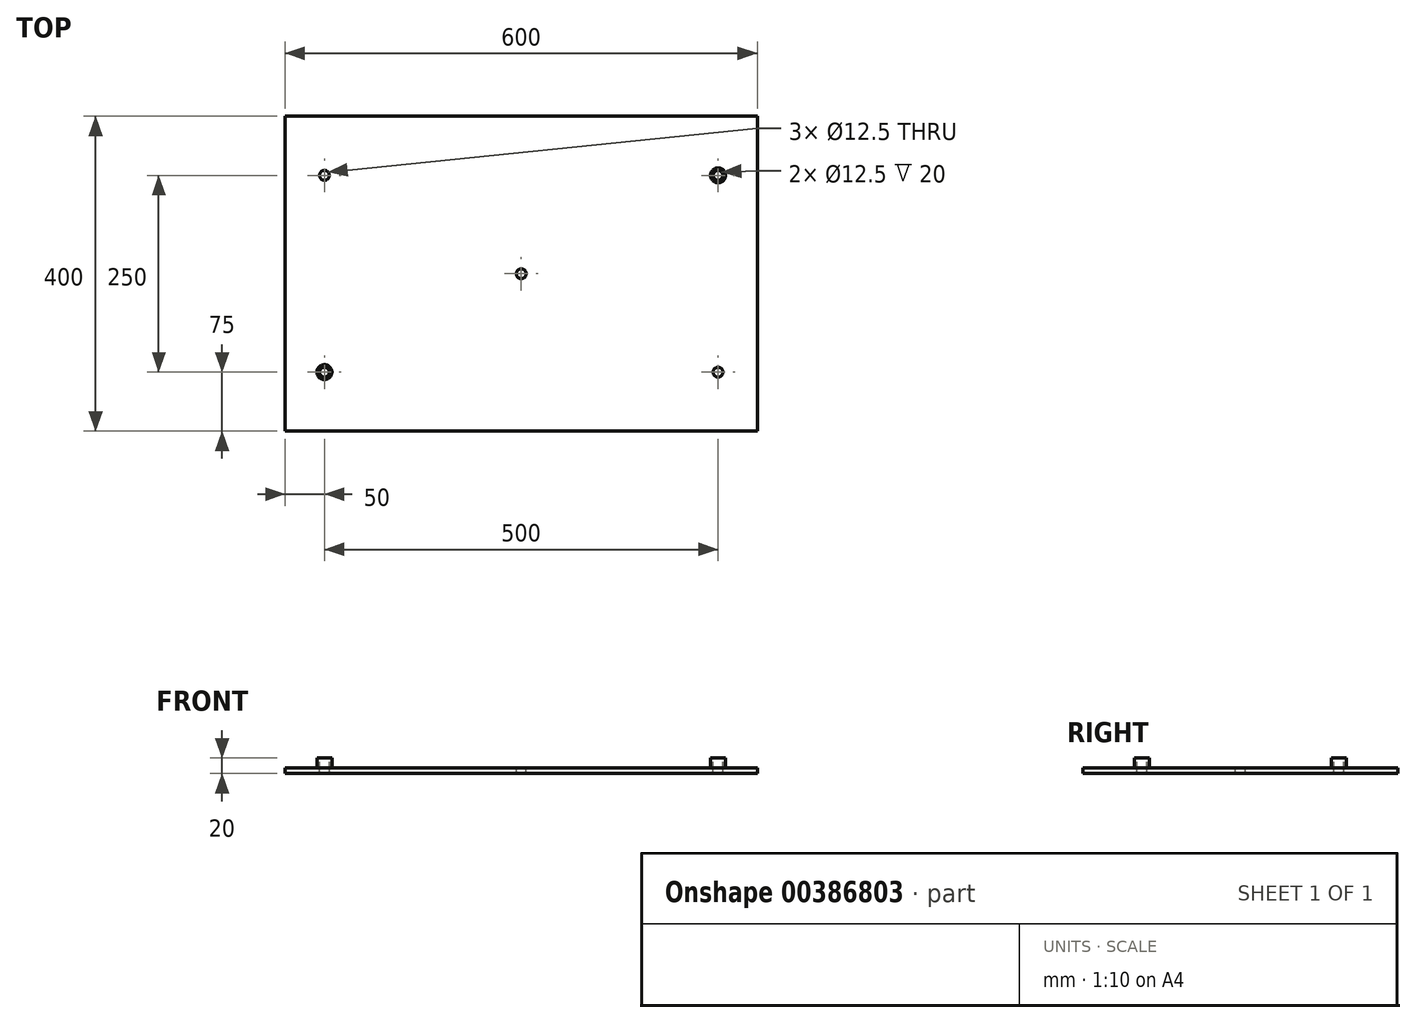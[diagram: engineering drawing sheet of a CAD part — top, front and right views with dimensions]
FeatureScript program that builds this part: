
annotation { "Feature Type Name" : "Feature", "Feature Type Description" : "" }
export const myFeature = defineFeature(function(context is Context, id is Id, definition is map)
    precondition{}
    {
        {
            var Q0;
            Q0=qCreatedBy(makeId("Top.planeOp"),FACE);
            var sketch = newSketch(context, id + "F0", { "sketchPlane" : qUnion([Q0])});
            skLineSegment(sketch, "E0.bottom", {"start": v(300, -200) * mm, "end": v(-300, -200) * mm});
            skLineSegment(sketch, "E0.top", {"start": v(300, 200) * mm, "end": v(-300, 200) * mm});
            skLineSegment(sketch, "E0.left", {"start": v(300, -200) * mm, "end": v(300, 200) * mm});
            skLineSegment(sketch, "E0.right", {"start": v(-300, -200) * mm, "end": v(-300, 200) * mm});
            skPoint(sketch, "E0.middle", {"position": v(0, 0) * mm});
            skSolve(sketch);
        }
        {
            var Q0;
            Q0=makeQuery(id+"F0.imprint","IMPRINT",FACE,{"disambiguationData":[TD([[makeQuery(id+"F0.imprint","IMPRINT",EDGE,{"derivedFrom":sQuery(id+"F0.wireOp",EDGE,"E0.bottom")}),-1.0]])]});
            extrude(context, id + "F1", {"entities" : qUnion([Q0]), "depth" : 20 * mm});
        }
        {
            var Q0;
            Q0=makeQuery(id+"F1.opExtrude","CAP_FACE",FACE,{"disambiguationData":[OSD([sQuery(id+"F0.wireOp",EDGE,"E0.bottom"),sQuery(id+"F0.wireOp",EDGE,"E0.top"),sQuery(id+"F0.wireOp",EDGE,"E0.left"),sQuery(id+"F0.wireOp",EDGE,"E0.right")])],"isStart":false});
            var sketch = newSketch(context, id + "F2", { "sketchPlane" : qUnion([Q0])});
            skCircle(sketch, "E1", {"center": v(-250, 125) * mm, "radius": 6.25 * mm});
            skCircle(sketch, "E2", {"center": v(-250, -125) * mm, "radius": 6.25 * mm});
            skCircle(sketch, "E3", {"center": v(0, 0) * mm, "radius": 6.25 * mm});
            skCircle(sketch, "E4", {"center": v(250, 125) * mm, "radius": 6.25 * mm});
            skCircle(sketch, "E5", {"center": v(250, -125) * mm, "radius": 6.25 * mm});
            skSolve(sketch);
        }
        {
            var Q0;
            Q0=makeQuery(id+"F2.imprint","IMPRINT",FACE,{"disambiguationData":[TD([[makeQuery(id+"F2.imprint","IMPRINT",EDGE,{"derivedFrom":sQuery(id+"F2.wireOp",EDGE,"E1")}),1.0]])]});
            var Q1;
            Q1=makeQuery(id+"F2.imprint","IMPRINT",FACE,{"disambiguationData":[TD([[makeQuery(id+"F2.imprint","IMPRINT",EDGE,{"derivedFrom":sQuery(id+"F2.wireOp",EDGE,"E2")}),1.0]])]});
            var Q2;
            Q2=makeQuery(id+"F2.imprint","IMPRINT",FACE,{"disambiguationData":[TD([[makeQuery(id+"F2.imprint","IMPRINT",EDGE,{"derivedFrom":sQuery(id+"F2.wireOp",EDGE,"E4")}),1.0]])]});
            var Q3;
            Q3=makeQuery(id+"F2.imprint","IMPRINT",FACE,{"disambiguationData":[TD([[makeQuery(id+"F2.imprint","IMPRINT",EDGE,{"derivedFrom":sQuery(id+"F2.wireOp",EDGE,"E5")}),1.0]])]});
            var Q4;
            Q4=makeQuery(id+"F2.imprint","IMPRINT",FACE,{"disambiguationData":[TD([[makeQuery(id+"F2.imprint","IMPRINT",EDGE,{"derivedFrom":sQuery(id+"F2.wireOp",EDGE,"E3")}),1.0]])]});
            extrude(context, id + "F3", {"entities" : qUnion([Q0, Q1, Q2, Q3, Q4]), "operationType" : NewBodyOperationType.REMOVE, "oppositeDirection" : true, "depth" : 25 * mm});
        }
        {
            var Q0;
            Q0=makeQuery(id+"F1.opExtrude","CAP_FACE",FACE,{"disambiguationData":[OSD([sQuery(id+"F0.wireOp",EDGE,"E0.bottom"),sQuery(id+"F0.wireOp",EDGE,"E0.top"),sQuery(id+"F0.wireOp",EDGE,"E0.left"),sQuery(id+"F0.wireOp",EDGE,"E0.right")])],"isStart":false});
            var sketch = newSketch(context, id + "F4", { "sketchPlane" : qUnion([Q0])});
            skCircle(sketch, "E6", {"center": v(-250, 125) * mm, "radius": 9.5 * mm});
            skCircle(sketch, "E7.MirrorC", {"center": v(250, 125) * mm, "radius": 9.5 * mm});
            skCircle(sketch, "E8.MirrorC", {"center": v(-250, -125) * mm, "radius": 9.5 * mm});
            skCircle(sketch, "E9.MirrorC", {"center": v(250, -125) * mm, "radius": 9.5 * mm});
            skCircle(sketch, "E10", {"center": v(0, 0) * mm, "radius": 9.5 * mm});
            skSolve(sketch);
        }
        {
            var Q0;
            Q0=makeQuery(id+"F4.imprint","IMPRINT",FACE,{"disambiguationData":[TD([[makeQuery(id+"F4.imprint","IMPRINT",EDGE,{"derivedFrom":sQuery(id+"F4.wireOp",EDGE,"E7.MirrorC")}),-1.0]])]});
            var Q1;
            Q1=makeQuery(id+"F4.imprint","IMPRINT",FACE,{"disambiguationData":[TD([[makeQuery(id+"F4.imprint","IMPRINT",EDGE,{"derivedFrom":sQuery(id+"F4.wireOp",EDGE,"E9.MirrorC")}),1.0]])]});
            var Q2;
            Q2=makeQuery(id+"F4.imprint","IMPRINT",FACE,{"disambiguationData":[TD([[makeQuery(id+"F4.imprint","IMPRINT",EDGE,{"derivedFrom":sQuery(id+"F4.wireOp",EDGE,"E10")}),1.0]])]});
            var Q3;
            Q3=makeQuery(id+"F4.imprint","IMPRINT",FACE,{"disambiguationData":[TD([[makeQuery(id+"F4.imprint","IMPRINT",EDGE,{"derivedFrom":sQuery(id+"F4.wireOp",EDGE,"E6")}),1.0]])]});
            var Q4;
            Q4=makeQuery(id+"F4.imprint","IMPRINT",FACE,{"disambiguationData":[TD([[makeQuery(id+"F4.imprint","IMPRINT",EDGE,{"derivedFrom":sQuery(id+"F4.wireOp",EDGE,"E8.MirrorC")}),-1.0]])]});
            extrude(context, id + "F5", {"entities" : qUnion([Q0, Q1, Q2, Q3, Q4]), "operationType" : NewBodyOperationType.REMOVE, "oppositeDirection" : true, "depth" : 13 * mm});
        }
    });
